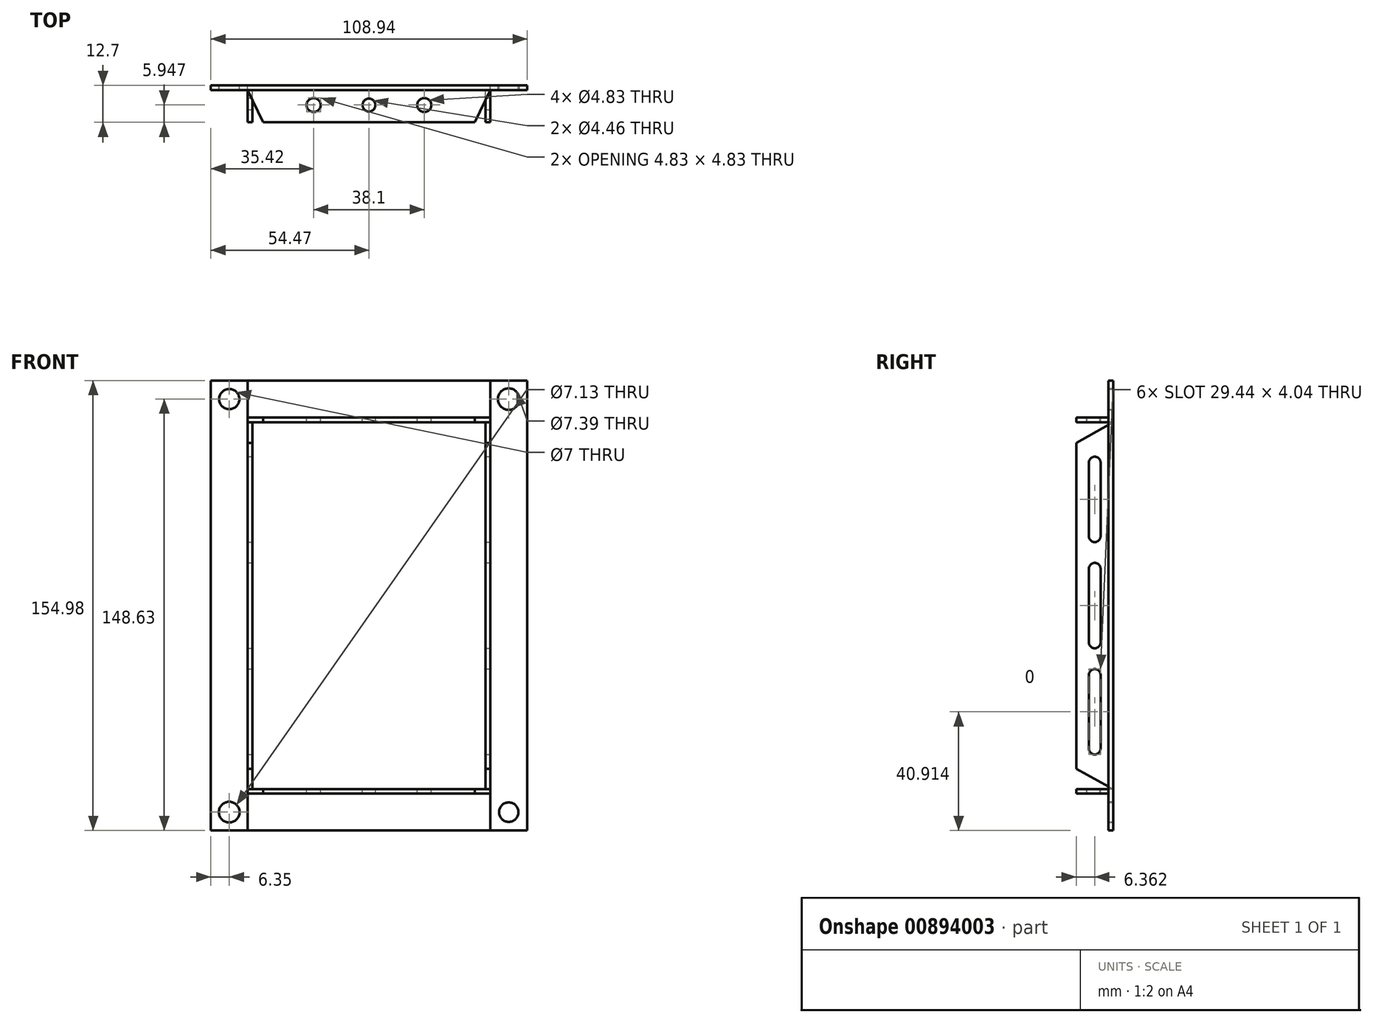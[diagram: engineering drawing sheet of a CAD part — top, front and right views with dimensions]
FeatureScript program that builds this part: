
annotation { "Feature Type Name" : "Feature", "Feature Type Description" : "" }
export const myFeature = defineFeature(function(context is Context, id is Id, definition is map)
    precondition{}
    {
        {
            var Q0;
            Q0=qCreatedBy(makeId("Front.planeOp"),FACE);
            var sketch = newSketch(context, id + "F0", { "sketchPlane" : qUnion([Q0])});
            skLineSegment(sketch, "E0.bottom", {"start": v(54.47, 77.5) * mm, "end": v(-54.47, 77.5) * mm});
            skLineSegment(sketch, "E0.top", {"start": v(54.47, -77.5) * mm, "end": v(-54.47, -77.5) * mm});
            skLineSegment(sketch, "E0.left", {"start": v(54.47, 77.5) * mm, "end": v(54.47, -77.5) * mm});
            skLineSegment(sketch, "E0.right", {"start": v(-54.47, 77.5) * mm, "end": v(-54.47, -77.5) * mm});
            skPoint(sketch, "E0.middle", {"position": v(0, 0) * mm});
            skLineSegment(sketch, "E1.bottom", {"start": v(41.77, 64.8) * mm, "end": v(-41.77, 64.8) * mm});
            skLineSegment(sketch, "E1.top", {"start": v(41.77, -64.8) * mm, "end": v(-41.77, -64.8) * mm});
            skLineSegment(sketch, "E1.left", {"start": v(41.77, 64.8) * mm, "end": v(41.77, -64.8) * mm});
            skLineSegment(sketch, "E1.right", {"start": v(-41.77, 64.8) * mm, "end": v(-41.77, -64.8) * mm});
            skCircle(sketch, "E2", {"center": v(-48.12, 71.14) * mm, "radius": 3.5 * mm});
            skCircle(sketch, "E3", {"center": v(48.12, 71.14) * mm, "radius": 3.7 * mm});
            skCircle(sketch, "E4", {"center": v(-48.12, -71.14) * mm, "radius": 3.56 * mm});
            skCircle(sketch, "E5", {"center": v(48.12, -71.14) * mm, "radius": 3.35 * mm});
            skSolve(sketch);
        }
        {
            var Q0;
            Q0 = qSketchRegion(id + "F0", true);
            extrude(context, id + "F1", {"entities" : qUnion([Q0]), "depth" : 1.59 * mm, "offsetDistance" : 25.4 * mm});
        }
        {
            var Q0;
            Q0=qCreatedBy(makeId("Right.planeOp"),FACE);
            var sketch = newSketch(context, id + "F2", { "sketchPlane" : qUnion([Q0])});
            skLineSegment(sketch, "E6", {"start": v(0, 64.78) * mm, "end": v(0, 63.2) * mm});
            skLineSegment(sketch, "E7", {"start": v(0, 63.2) * mm, "end": v(-12.7, 63.2) * mm});
            skLineSegment(sketch, "E8", {"start": v(-12.7, 63.2) * mm, "end": v(-12.7, 64.78) * mm});
            skLineSegment(sketch, "E9", {"start": v(-12.7, 64.78) * mm, "end": v(0, 64.78) * mm});
            skLineSegment(sketch, "E10.MirrorCS", {"start": v(-12.7, -63.2) * mm, "end": v(-12.7, -64.78) * mm});
            skLineSegment(sketch, "E11.MirrorCS", {"start": v(0, -64.78) * mm, "end": v(0, -63.2) * mm});
            skLineSegment(sketch, "E12.MirrorCS", {"start": v(0, -63.2) * mm, "end": v(-12.7, -63.2) * mm});
            skLineSegment(sketch, "E13.MirrorCS", {"start": v(-12.7, -64.78) * mm, "end": v(0, -64.78) * mm});
            skSolve(sketch);
        }
        {
            var Q0;
            Q0 = qSketchRegion(id + "F2", true);
            extrude(context, id + "F3", {"entities" : qUnion([Q0]), "operationType" : NewBodyOperationType.ADD, "endBound" : BoundingType.SYMMETRIC, "oppositeDirection" : true, "depth" : 83.62 * mm, "offsetDistance" : 25.4 * mm});
        }
        {
            var Q0;
            Q0=qCreatedBy(makeId("Top.planeOp"),FACE);
            var sketch = newSketch(context, id + "F4", { "sketchPlane" : qUnion([Q0])});
            skLineSegment(sketch, "E14", {"start": v(-41.8, -1.43) * mm, "end": v(-35.6, -14.55) * mm});
            skLineSegment(sketch, "E15", {"start": v(-35.6, -14.55) * mm, "end": v(-41.81, -14.55) * mm});
            skLineSegment(sketch, "E16", {"start": v(-41.81, -14.55) * mm, "end": v(-41.8, -1.43) * mm});
            skLineSegment(sketch, "E17.MirrorCS", {"start": v(41.81, -14.55) * mm, "end": v(41.8, -1.43) * mm});
            skLineSegment(sketch, "E18.MirrorCS", {"start": v(35.6, -14.55) * mm, "end": v(41.81, -14.55) * mm});
            skLineSegment(sketch, "E19.MirrorCS", {"start": v(41.8, -1.43) * mm, "end": v(35.6, -14.55) * mm});
            skCircle(sketch, "E20", {"center": v(0, -6.75) * mm, "radius": 2.23 * mm});
            skCircle(sketch, "E21", {"center": v(-19.05, -6.75) * mm, "radius": 2.41 * mm});
            skCircle(sketch, "E22.MirrorC", {"center": v(19.05, -6.75) * mm, "radius": 2.41 * mm});
            skSolve(sketch);
        }
        {
            var Q0;
            Q0 = qSketchRegion(id + "F4", true);
            extrude(context, id + "F5", {"entities" : qUnion([Q0]), "operationType" : NewBodyOperationType.REMOVE, "endBound" : BoundingType.SYMMETRIC, "oppositeDirection" : true, "depth" : 163.58 * mm, "offsetDistance" : 25.4 * mm});
        }
        {
            var Q0;
            Q0=qCreatedBy(makeId("Right.planeOp"),FACE);
            var sketch = newSketch(context, id + "F6", { "sketchPlane" : qUnion([Q0])});
            skLineSegment(sketch, "E23.left", {"start": v(0, 63.2) * mm, "end": v(0, -63.2) * mm});
            skLineSegment(sketch, "E23.right", {"start": v(-12.7, 56) * mm, "end": v(-12.7, -56.25) * mm});
            skLineSegment(sketch, "E24.left", {"start": v(-4.32, 12.7) * mm, "end": v(-4.32, -12.7) * mm});
            skLineSegment(sketch, "E24.right", {"start": v(-8.36, 12.7) * mm, "end": v(-8.36, -12.7) * mm});
            skPoint(sketch, "E24.middle", {"position": v(-6.34, 0) * mm});
            skArc(sketch, "E25", {"start": v(-8.36, 12.7) * mm, "mid": v(-6.34, 14.72) * mm, "end": v(-4.32, 12.7) * mm});
            skArc(sketch, "E26", {"start": v(-8.36, -12.7) * mm, "mid": v(-6.34, -14.72) * mm, "end": v(-4.32, -12.7) * mm});
            skArc(sketch, "E27.1.0.0", {"start": v(-8.36, -49.28) * mm, "mid": v(-6.34, -51.3) * mm, "end": v(-4.32, -49.28) * mm});
            skLineSegment(sketch, "E27.1.0.1", {"start": v(-4.32, -23.88) * mm, "end": v(-4.32, -49.28) * mm});
            skPoint(sketch, "E27.1.0.2", {"position": v(-6.34, -36.58) * mm});
            skLineSegment(sketch, "E27.1.0.3", {"start": v(-8.36, -23.88) * mm, "end": v(-8.36, -49.28) * mm});
            skArc(sketch, "E27.1.0.4", {"start": v(-8.36, -23.88) * mm, "mid": v(-6.34, -21.86) * mm, "end": v(-4.32, -23.88) * mm});
            skLineSegment(sketch, "E27.direction1", {"start": v(-8.36, -12.7) * mm, "end": v(-8.36, -49.28) * mm, "construction": true});
            skArc(sketch, "E28.MirrorCS", {"start": v(-8.36, 49.28) * mm, "mid": v(-6.34, 51.3) * mm, "end": v(-4.32, 49.28) * mm});
            skLineSegment(sketch, "E29.MirrorCS", {"start": v(-8.36, 23.88) * mm, "end": v(-8.36, 49.28) * mm});
            skLineSegment(sketch, "E30.MirrorCS", {"start": v(-4.32, 23.88) * mm, "end": v(-4.32, 49.28) * mm});
            skArc(sketch, "E31.MirrorCS", {"start": v(-8.36, 23.88) * mm, "mid": v(-6.34, 21.86) * mm, "end": v(-4.32, 23.88) * mm});
            skPoint(sketch, "E32.MirrorP", {"position": v(-6.34, 36.58) * mm});
            skLineSegment(sketch, "E33", {"start": v(0, 63.2) * mm, "end": v(-12.7, 56) * mm});
            skLineSegment(sketch, "E34", {"start": v(0, -63.2) * mm, "end": v(-12.7, -56.25) * mm});
            skSolve(sketch);
        }
        {
            var Q0;
            Q0 = qSketchRegion(id + "F6", true);
            var Q1;
            {var subQ4=sQuery(id+"F0.wireOp",EDGE,"E1.right");Q1=makeQuery(id+"F3.boolean.opBoolean","SPLIT",FACE,{"disambiguationData":[TD([makeQuery(id+"F3.opExtrude","SWEPT_FACE",FACE,{"disambiguationData":[OSD([sQuery(id+"F2.wireOp",EDGE,"E7")])]})])],"derivedFrom":makeQuery(id+"F1.opExtrude","SWEPT_FACE",FACE,{"disambiguationData":[OSD([subQ4])]})});}
            var Q2;
            {var subQ5=sQuery(id+"F0.wireOp",EDGE,"E1.left");Q2=makeQuery(id+"F3.boolean.opBoolean","SPLIT",FACE,{"disambiguationData":[TD([makeQuery(id+"F3.opExtrude","SWEPT_FACE",FACE,{"disambiguationData":[OSD([sQuery(id+"F2.wireOp",EDGE,"E7")])]})])],"derivedFrom":makeQuery(id+"F1.opExtrude","SWEPT_FACE",FACE,{"disambiguationData":[OSD([subQ5])]})});}
            extrude(context, id + "F7", {"entities" : qUnion([Q0]), "endBound" : BoundingType.UP_TO_SURFACE, "oppositeDirection" : true, "depth" : 67.92 * mm, "endBoundEntityFace" : qUnion([Q1]), "offsetDistance" : 25.4 * mm, "hasSecondDirection" : true, "secondDirectionBound" : SecondDirectionBoundingType.UP_TO_SURFACE, "secondDirectionOppositeDirection" : false, "secondDirectionDepth" : 25.4 * mm, "secondDirectionBoundEntityFace" : qUnion([Q2])});
        }
        {
            var Q0;
            Q0=qCreatedBy(makeId("Front.planeOp"),FACE);
            var sketch = newSketch(context, id + "F8", { "sketchPlane" : qUnion([Q0])});
            skLineSegment(sketch, "E35.bottom", {"start": v(40.18, 63.2) * mm, "end": v(-40.18, 63.2) * mm});
            skLineSegment(sketch, "E35.top", {"start": v(40.18, -63.2) * mm, "end": v(-40.18, -63.2) * mm});
            skLineSegment(sketch, "E35.left", {"start": v(40.18, 63.2) * mm, "end": v(40.18, -63.2) * mm});
            skLineSegment(sketch, "E35.right", {"start": v(-40.18, 63.2) * mm, "end": v(-40.18, -63.2) * mm});
            skPoint(sketch, "E35.middle", {"position": v(0, 0) * mm});
            skSolve(sketch);
        }
        {
            var Q0;
            Q0 = qSketchRegion(id + "F8", true);
            extrude(context, id + "F9", {"entities" : qUnion([Q0]), "operationType" : NewBodyOperationType.REMOVE, "endBound" : BoundingType.THROUGH_ALL, "depth" : 25.4 * mm, "offsetDistance" : 25.4 * mm});
        }
    });
